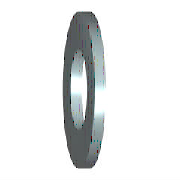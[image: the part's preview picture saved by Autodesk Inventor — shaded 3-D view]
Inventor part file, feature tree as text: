
AUTODESK INVENTOR PART (.ipt)
format: ipt  version: 2020 (Build 240168000, 168)  size: 109,568 bytes
history: native  units: mm (DEFAULTED — no unit token found)
features: other x1, plane x1, sketch x1
ambient origin geometry x7: Origin, YZ Plane, XY Plane, X Axis, Y Axis, Z Axis, Center Point
bodies: Solid1 (feature_tree), Body (feature_tree)
feature tree (3):
  other  "Work Axis1"
  plane  "Work Plane1"
  sketch  "Sketch"  dims[d0=3.2mm d1=7.0mm d2=0.5mm d3=0.0mm d4=0.0mm d5=0.0mm d6=0.0mm d7=0.0mm]
